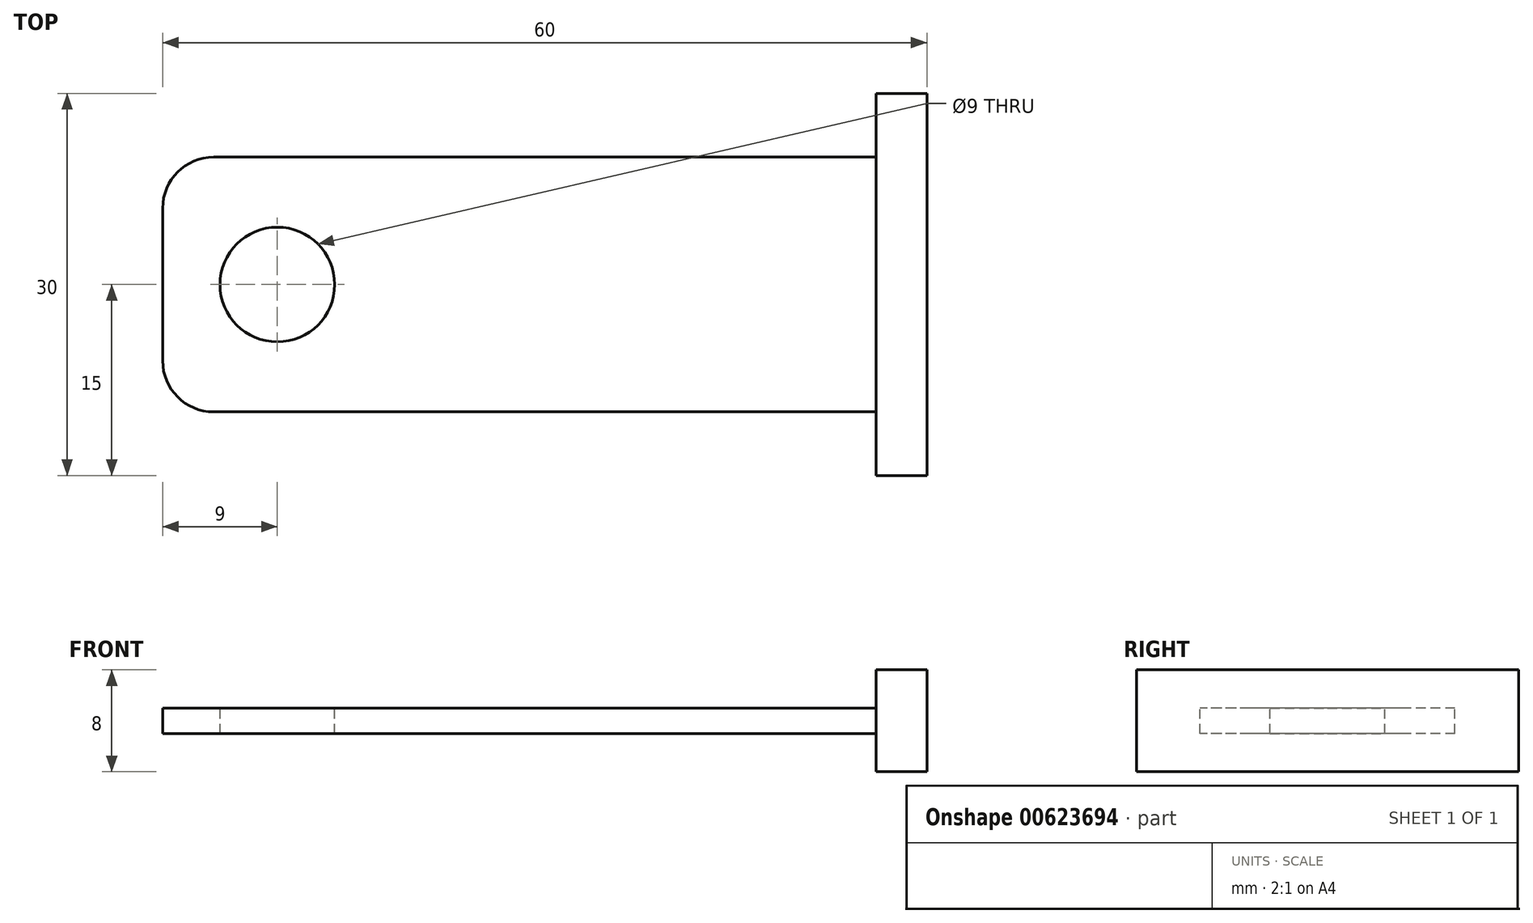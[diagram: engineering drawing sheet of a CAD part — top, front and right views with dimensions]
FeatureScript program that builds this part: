
annotation { "Feature Type Name" : "Feature", "Feature Type Description" : "" }
export const myFeature = defineFeature(function(context is Context, id is Id, definition is map)
    precondition{}
    {
        {
            var Q0;
            Q0=qCreatedBy(makeId("Top.planeOp"),FACE);
            var sketch = newSketch(context, id + "F0", { "sketchPlane" : qUnion([Q0])});
            skLineSegment(sketch, "E0.bottom", {"start": v(28, 10) * mm, "end": v(-28, 10) * mm});
            skLineSegment(sketch, "E0.top", {"start": v(28, -10) * mm, "end": v(-28, -10) * mm});
            skLineSegment(sketch, "E0.left", {"start": v(28, 10) * mm, "end": v(28, -10) * mm});
            skLineSegment(sketch, "E0.right", {"start": v(-28, 10) * mm, "end": v(-28, -10) * mm});
            skPoint(sketch, "E0.middle", {"position": v(0, 0) * mm});
            skLineSegment(sketch, "E1.bottom", {"start": v(28, 15) * mm, "end": v(32, 15) * mm});
            skLineSegment(sketch, "E1.top", {"start": v(28, -15) * mm, "end": v(32, -15) * mm});
            skLineSegment(sketch, "E1.left", {"start": v(28, 15) * mm, "end": v(28, -15) * mm});
            skLineSegment(sketch, "E1.right", {"start": v(32, 15) * mm, "end": v(32, -15) * mm});
            skPoint(sketch, "E1.middle", {"position": v(30, 0) * mm});
            skPoint(sketch, "E1.middle.positionSnap0", {"position": v(28, 0) * mm});
            skPoint(sketch, "E1.centerSnap0", {"position": v(28, 0) * mm});
            skCircle(sketch, "E2", {"center": v(-19, 0) * mm, "radius": 4.5 * mm});
            skSolve(sketch);
        }
        {
            var Q0;
            {var subQ3=sQuery(id+"F0.wireOp",EDGE,"E1.bottom");Q0=makeQuery(id+"F0.imprint","IMPRINT",FACE,{"disambiguationData":[TD([[makeQuery(id+"F0.imprint","IMPRINT",EDGE,{"derivedFrom":subQ3}),-1.0]])]});}
            extrude(context, id + "F1", {"entities" : qUnion([Q0]), "endBound" : BoundingType.SYMMETRIC, "depth" : 8 * mm, "offsetDistance" : 25 * mm});
        }
        {
            var Q0;
            {var subQ1=sQuery(id+"F0.wireOp",EDGE,"E0.bottom");Q0=makeQuery(id+"F0.imprint","IMPRINT",FACE,{"disambiguationData":[TD([[makeQuery(id+"F0.imprint","IMPRINT",EDGE,{"derivedFrom":subQ1}),1.0]])]});}
            extrude(context, id + "F2", {"entities" : qUnion([Q0]), "endBound" : BoundingType.SYMMETRIC, "oppositeDirection" : true, "depth" : 2 * mm, "offsetDistance" : 25 * mm});
        }
        {
            var Q0;
            Q0=makeQuery(id+"F2.opExtrude","SWEPT_EDGE",EDGE,{"disambiguationData":[OSD([sQuery(id+"F0.wireOp",EDGE,"E0.top"),sQuery(id+"F0.wireOp",EDGE,"E0.right")])]});
            fillet(context, id + "F3", {"entities" : qUnion([Q0]), "radius" : 4 * mm, "tangentPropagation" : true, "allowEdgeOverflow" : false});
        }
        {
            var Q0;
            Q0=makeQuery(id+"F2.opExtrude","SWEPT_EDGE",EDGE,{"disambiguationData":[OSD([sQuery(id+"F0.wireOp",EDGE,"E0.bottom"),sQuery(id+"F0.wireOp",EDGE,"E0.right")])]});
            fillet(context, id + "F4", {"entities" : qUnion([Q0]), "radius" : 4 * mm, "tangentPropagation" : true, "allowEdgeOverflow" : false});
        }
    });
